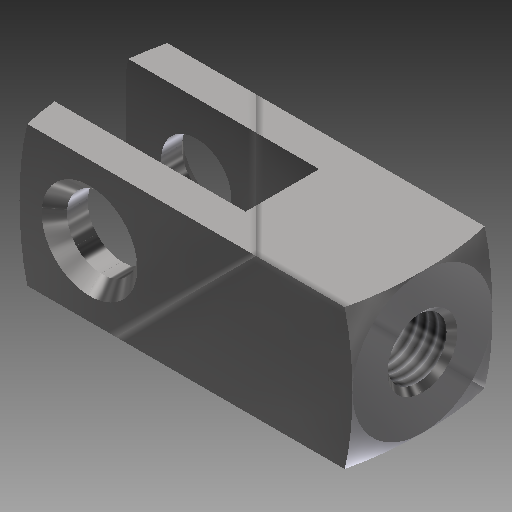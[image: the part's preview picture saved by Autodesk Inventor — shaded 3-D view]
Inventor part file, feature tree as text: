
AUTODESK INVENTOR PART (.ipt)
format: ipt  version: 2017 (Build 210142000, 142)  size: 243,200 bytes
history: native  units: in
note: dims shown in document units (in); Inventor stores cm internally (conversion verified against a paired STEP export)
features: other x126, sketch x7, revolve x4, extrude x2, thread x1, hole x1
ambient origin geometry x8: Origin, YZ Plane, XZ Plane, XY Plane, X Axis, Y Axis, Z Axis, Center Point
bodies: Solid1 (feature_tree)
feature tree (141):
  extrude  "Extrusion1"  Depth=0.5in TaperAngle=0.0deg
  extrude  "Extrusion2"  Depth=0.4207in TaperAngle=0.0deg
  revolve  "Revolution1"  Angle=360.0deg
  thread  "Thread1"  [1 undecoded]
  hole  "Hole1"  [1 undecoded]
  revolve  "Revolution2"  [1 undecoded]
  revolve  "Revolution3"  [1 undecoded]
  revolve  "Revolution4"  [1 undecoded]
  other  "dummy_XY"
  other  "dummy_YZ"
  other  "dummy_ZX"
  other  "dummy_X"
  other  "dummy_Y"
  other  "dummy_Z"
  other  "dummy_Center"
  other  "h1_XY"
  other  "h1_YZ"
  other  "h1_ZX"
  other  "h1_X"
  other  "h1_Y"
  other  "h1_Z"
  other  "h1_Center"
  other  "h2_XY"
  other  "h2_YZ"
  other  "h2_ZX"
  other  "h2_X"
  other  "h2_Y"
  other  "h2_Z"
  other  "h2_Center"
  other  "l1_XY"
  other  "l1_YZ"
  other  "l1_ZX"
  other  "l1_X"
  other  "l1_Y"
  other  "l1_Z"
  other  "l1_Center"
  other  "l11_XY"
  other  "l11_YZ"
  other  "l11_ZX"
  other  "l11_X"
  other  "l11_Y"
  other  "l11_Z"
  other  "l11_Center"
  other  "l12_XY"
  other  "l12_YZ"
  other  "l12_ZX"
  other  "l12_X"
  other  "l12_Y"
  other  "l12_Z"
  other  "l12_Center"
  other  "l2_XY"
  other  "l2_YZ"
  other  "l2_ZX"
  other  "l2_X"
  other  "l2_Y"
  other  "l2_Z"
  other  "l2_Center"
  other  "l21_XY"
  other  "l21_YZ"
  other  "l21_ZX"
  other  "l21_X"
  other  "l21_Y"
  other  "l21_Z"
  other  "l21_Center"
  other  "l22_XY"
  other  "l22_YZ"
  other  "l22_ZX"
  other  "l22_X"
  other  "l22_Y"
  other  "l22_Z"
  other  "l22_Center"
  other  "piston_rod_clevis_XY"
  other  "piston_rod_clevis_YZ"
  other  "piston_rod_clevis_ZX"
  other  "piston_rod_clevis_X"
  other  "piston_rod_clevis_Y"
  other  "piston_rod_clevis_Z"
  other  "piston_rod_clevis_Center"
  other  "rod_clevis_body_XY"
  other  "rod_clevis_body_YZ"
  other  "rod_clevis_body_ZX"
  other  "rod_clevis_body_X"
  other  "rod_clevis_body_Y"
  other  "rod_clevis_body_Z"
  other  "rod_clevis_body_Center"
  other  "th1_XY"
  other  "th1_YZ"
  other  "th1_ZX"
  other  "th1_X"
  other  "th1_Y"
  other  "th1_Z"
  other  "th1_Center"
  other  "th2_XY"
  other  "th2_YZ"
  other  "th2_ZX"
  other  "th2_X"
  other  "th2_Y"
  other  "th2_Z"
  other  "th2_Center"
  other  "to_cylinder_XY"
  other  "to_cylinder_YZ"
  other  "to_cylinder_ZX"
  other  "to_cylinder_X"
  other  "to_cylinder_Y"
  other  "to_cylinder_Z"
  other  "to_cylinder_Center"
  other  "w1_XY"
  other  "w1_YZ"
  other  "w1_ZX"
  other  "w1_X"
  other  "w1_Y"
  other  "w1_Z"
  other  "w1_Center"
  other  "w11_XY"
  other  "w11_YZ"
  other  "w11_ZX"
  other  "w11_X"
  other  "w11_Y"
  other  "w11_Z"
  other  "w11_Center"
  other  "w12_XY"
  other  "w12_YZ"
  other  "w12_ZX"
  other  "w12_X"
  other  "w12_Y"
  other  "w12_Z"
  other  "w12_Center"
  other  "w2_XY"
  other  "w2_YZ"
  other  "w2_ZX"
  other  "w2_X"
  other  "w2_Y"
  other  "w2_Z"
  other  "w2_Center"
  sketch  "Sketch_1"  dims[d0=0.5in d1=0.0in d2=0.5in d3=0.0in]
  sketch  "Sketch_2"  dims[d4=360.0deg d5=0.4207in d6=0.0in]
  sketch  "Sketch_3"  dims[d7=0.213in d8=0.75in d9=0.375in d10=0.25in d11=0.5635in d12=0.06in d13=0.0in d14=360.0deg d15=360.0deg]
  sketch  "Sketch5"  dims[d16=360.0deg d17=0.0in d18=0.0in]
  sketch  "Sketch_5"
  sketch  "Sketch_9"
  sketch  "Sketch_10"
note: 5 required parameter values undecoded (feature->parameter linkage not recoverable at this tier; creation-order binding heuristic only, values carry confidence <= 0.55)
